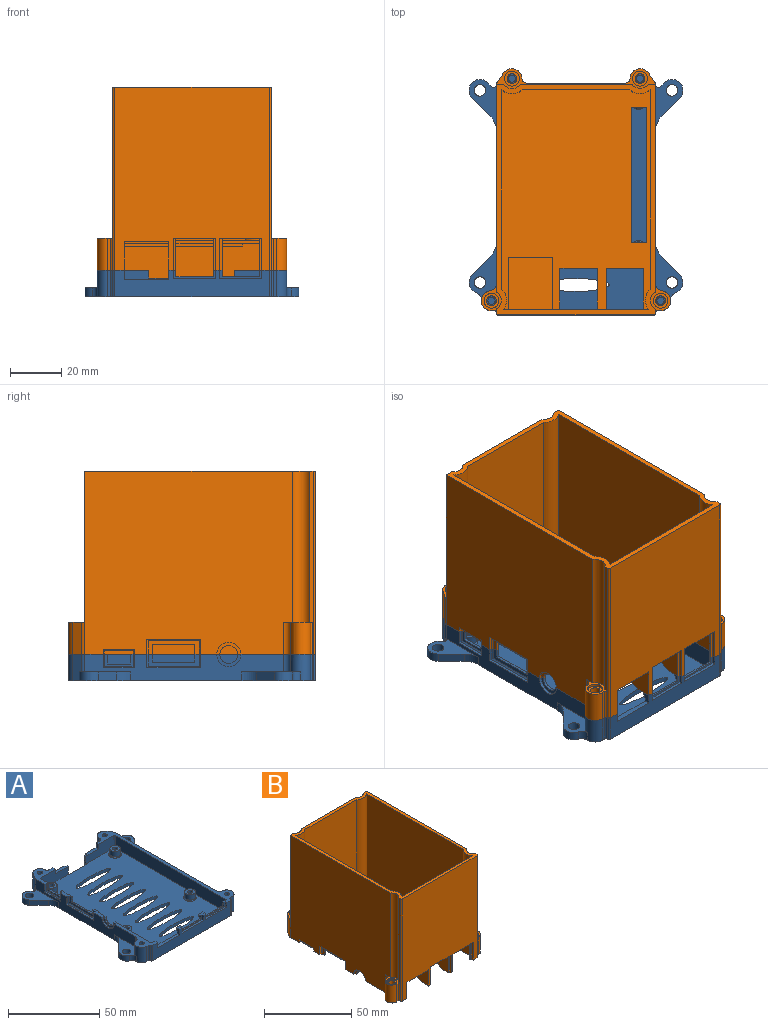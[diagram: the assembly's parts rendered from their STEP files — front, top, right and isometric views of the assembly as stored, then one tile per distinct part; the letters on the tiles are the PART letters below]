
ASSEMBLY  parts=2 mates=1
PART A: 170 faces, bbox 83.8x96.6x10.6 mm
  f0: plane 96.58x83.83mm, normal (0,0,-1), area 5317.9mm2, adj f1,f6,f7,f8,f9,f37,f38,f39
  f1: cylinder r=2.25mm len=4.5mm, axis (0,0,-1), area 49.5mm2, adj f0,f3
  f2: plane 22.79x10.75mm, normal (0,0,1), area 100.2mm2, adj f8,f9,f93,f123,f124,f125,f126,f127
  f3: plane 22.79x10.75mm, normal (0,0,1), area 100.2mm2, adj f1,f39,f152,f153,f154,f155,f156,f157
  f4: plane 20.07x10.76mm, normal (0,0,1), area 93.7mm2, adj f6,f39,f41,f147,f148,f149,f150,f151
  f5: plane 20.07x10.76mm, normal (0,0,1), area 93.7mm2, adj f7,f93,f128,f129,f130,f131,f132,f133
  f6: cylinder r=2.25mm len=4.5mm, axis (0,0,-1), area 49.5mm2, adj f0,f4
  f7: cylinder r=2.25mm len=4.5mm, axis (0,0,-1), area 49.5mm2, adj f0,f5
  f8: cylinder r=2.25mm len=4.5mm, axis (0,0,-1), area 49.5mm2, adj f0,f2
  f9: cylinder r=3.9mm len=10.3mm, axis (0,0,-1), area 101.4mm2, adj f0,f2,f12,f123,f127,f139
  f10: plane 3x2.8mm, normal (0,0,1), area 7.2mm2, adj f25,f28,f30,f37,f162,f163
  f11: plane 3.5x3mm, normal (0,0,1), area 8.1mm2, adj f29,f32,f35,f37,f163,f164,f167,f169
  f12: plane 30.25x10.45mm, normal (0,0,1), area 99.5mm2, adj f9,f22,f26,f37,f89,f90,f91,f92
  f13: plane 8.65x2.5mm, normal (0,0,1), area 15.1mm2, adj f89,f93,f95,f96,f97,f98,f100,f101
  f14: plane 9.75x2.5mm, normal (0,0,1), area 16.8mm2, adj f89,f90,f91,f92,f93,f98,f101,f107
  f15: plane 15.1x14.15mm, normal (0,0,1), area 78mm2, adj f17,f46,f82,f88,f89,f93,f97,f99
  f16: plane 96.25x20.25mm, normal (0,0,1), area 280.9mm2, adj f23,f24,f26,f34,f35,f36,f37,f38
  f17: cylinder r=1.4mm len=8.3mm, axis (0,0,-1), area 73mm2, adj f15,f20
  f18: plane 2.8x2.8mm, normal (0,0,1), area 6.2mm2, adj f22
  f19: plane 2.8x2.8mm, normal (0,0,1), area 6.2mm2, adj f23
  f20: plane 2.8x2.8mm, normal (0,0,1), area 6.2mm2, adj f17
  f21: plane 2.8x2.8mm, normal (0,0,1), area 6.2mm2, adj f24
  f22: cylinder r=1.4mm len=8.3mm, axis (0,0,-1), area 73mm2, adj f12,f18
  f23: cylinder r=1.4mm len=8.3mm, axis (0,0,1), area 73mm2, adj f16,f19
  f24: cylinder r=1.4mm len=8.3mm, axis (0,0,-1), area 73mm2, adj f16,f21
  f25: plane 3.6x3mm, normal (-1,0,0), area 8.7mm2, adj f10,f26,f27,f30,f37,f161
  f26: plane 57x8.3mm, normal (0,1,0), area 322.8mm2, adj f12,f16,f25,f27,f28,f31,f32,f33
  f27: plane 2.8x2mm, normal (0,0.89,-0.45), area 6.3mm2, adj f25,f26,f28,f30
  f28: plane 2.55x1.8mm, normal (1,0,0), area 3.5mm2, adj f10,f26,f27,f30,f163,f168
  f29: plane 3.5x0.55mm, normal (0,1,0), area 1.9mm2, adj f11,f31,f32,f169
  f30: plane 2.8x0.55mm, normal (0,1,0), area 1.5mm2, adj f10,f25,f27,f28
  f31: plane 3.5x2mm, normal (0,0.89,-0.45), area 7.8mm2, adj f26,f29,f32,f169
  f32: plane 2.55x1.8mm, normal (1,0,0), area 3.5mm2, adj f11,f26,f29,f31,f33,f35
  f33: plane 14.5x0.8mm, normal (0,0,1), area 11.6mm2, adj f26,f32,f34,f35
  f34: plane 2.47x0.8mm, normal (-1,0,0), area 2mm2, adj f16,f26,f33,f35
  f35: plane 16.5x3.17mm, normal (0,-1,0), area 16.5mm2, adj f11,f16,f32,f33,f34,f36,f166,f167
  f36: plane 3.17x1.2mm, normal (-1,0,0), area 3.8mm2, adj f16,f35,f37,f166
  f37: plane 60.4x10.3mm, normal (0,-1,0), area 454.9mm2, adj f0,f10,f11,f12,f16,f25,f36,f38
  f38: cylinder r=0.8mm len=10.3mm, axis (0,0,-1), area 12.9mm2, adj f0,f16,f37,f40
  f39: plane 77.46x10.3mm, normal (1,0,0), area 678.5mm2, adj f0,f3,f4,f16,f41,f151,f152,f157
  f40: plane 10.3x0.18mm, normal (1,0,0), area 1.9mm2, adj f0,f16,f38,f159
  f41: cylinder r=2mm len=10.3mm, axis (0,0,1), area 12.1mm2, adj f0,f4,f16,f39,f42,f147
  f42: plane 10.3x3.48mm, normal (0.82,0.58,0), area 43.8mm2, adj f0,f16,f41,f43
  f43: cylinder r=3.9mm len=10.3mm, axis (0,0,-1), area 99.9mm2, adj f0,f16,f42,f44
  f44: cylinder r=2mm len=10.3mm, axis (0,0,1), area 31.5mm2, adj f0,f16,f43,f45
  f45: plane 10.96x10.3mm, normal (0,1,0), area 87.3mm2, adj f0,f16,f44,f47,f83,f84
  f46: plane 10.76x10.3mm, normal (0,1,0), area 85.3mm2, adj f0,f15,f136,f141,f142,f146
  f47: plane 7.3x1mm, normal (-1,0,0), area 7.3mm2, adj f0,f45,f48,f83
  f48: plane 7.3x1.5mm, normal (0,1,0), area 10.9mm2, adj f0,f47,f50,f83
  f49: plane 7.3x1.5mm, normal (0,1,0), area 11mm2, adj f0,f142,f143,f146
  f50: plane 7.3x1mm, normal (-1,0,0), area 7.3mm2, adj f0,f48,f51,f81,f83
  f51: cylinder r=0.5mm len=2mm, axis (0,0,-1), area 1.6mm2, adj f0,f50,f52,f145
  f52: plane 86.93x58.33mm, normal (0,0,1), area 4054.4mm2, adj f26,f51,f53,f54,f55,f56,f57,f58
  f53: extruded ~26x5mm, area 109.1mm2, adj f0,f52
  f54: extruded ~26x5mm, area 109.1mm2, adj f0,f52
  f55: extruded ~26x5mm, area 109.1mm2, adj f0,f52
  f56: extruded ~26x5mm, area 109.1mm2, adj f0,f52
  f57: extruded ~26x5mm, area 109.1mm2, adj f0,f52
  f58: extruded ~26x5mm, area 109.1mm2, adj f0,f52
  f59: extruded ~26x5mm, area 109.1mm2, adj f0,f52
  f60: extruded ~26x5mm, area 109.1mm2, adj f0,f52
  f61: cone r=3.15mm half-angle=45deg, axis (0,0,-1), area 14mm2, adj f52,f62
  f62: cylinder r=2.9mm len=5.8mm, axis (0,0,1), area 63.8mm2, adj f61,f64
  f63: plane 5.8x5.8mm, normal (0,0,1), area 20.3mm2, adj f67,f69
  f64: plane 5.8x5.8mm, normal (0,0,1), area 20.3mm2, adj f62,f74
  f65: plane 5.8x5.8mm, normal (0,0,1), area 20.3mm2, adj f76,f77
  f66: plane 5.8x5.8mm, normal (0,0,1), area 20.3mm2, adj f75,f79
  f67: cylinder r=2.9mm len=5.8mm, axis (0,0,1), area 63.8mm2, adj f63,f68
  f68: cone r=3.15mm half-angle=45deg, axis (0,0,-1), area 14mm2, adj f52,f67
  f69: cylinder r=1.4mm len=5mm, axis (0,0,1), area 44mm2, adj f63,f72
  f70: plane 2.8x2.8mm, normal (0,0,1), area 6.2mm2, adj f74
  f71: plane 2.8x2.8mm, normal (0,0,1), area 6.2mm2, adj f75
  f72: plane 2.8x2.8mm, normal (0,0,1), area 6.2mm2, adj f69
  f73: plane 2.8x2.8mm, normal (0,0,1), area 6.2mm2, adj f76
  f74: cylinder r=1.4mm len=5mm, axis (0,0,1), area 44mm2, adj f64,f70
  f75: cylinder r=1.4mm len=5mm, axis (0,0,1), area 44mm2, adj f66,f71
  f76: cylinder r=1.4mm len=5mm, axis (0,0,1), area 44mm2, adj f65,f73
  f77: cylinder r=2.9mm len=5.8mm, axis (0,0,1), area 63.8mm2, adj f65,f78
  f78: cone r=3.15mm half-angle=45deg, axis (0,0,-1), area 14mm2, adj f52,f77
  f79: cylinder r=2.9mm len=5.8mm, axis (0,0,1), area 63.8mm2, adj f66,f80
  f80: cone r=3.15mm half-angle=45deg, axis (0,0,-1), area 14mm2, adj f52,f79
  f81: plane 21.85x8.3mm, normal (0,-1,0), area 151.4mm2, adj f16,f50,f52,f83,f84,f85
  f82: plane 21.65x8.3mm, normal (0,-1,0), area 149.7mm2, adj f15,f52,f88,f141,f142,f143
  f83: plane 10x2mm, normal (0,0,1), area 18.5mm2, adj f45,f47,f48,f50,f81,f84
  f84: plane 3x2mm, normal (-1,0,0), area 6mm2, adj f16,f45,f81,f83
  f85: cylinder r=0.5mm len=8.3mm, axis (0,0,1), area 6.5mm2, adj f16,f52,f81,f86
  f86: plane 85.6x8.3mm, normal (-1,0,0), area 710.5mm2, adj f16,f52,f85,f87
  f87: cylinder r=0.5mm len=8.3mm, axis (0,0,1), area 6.5mm2, adj f16,f26,f52,f86
  f88: cylinder r=0.5mm len=8.3mm, axis (0,0,1), area 6.5mm2, adj f15,f52,f82,f89
  f89: plane 85.6x8.3mm, normal (1,0,0), area 494.1mm2, adj f12,f13,f14,f15,f52,f88,f90,f102
  f90: cylinder r=3.5mm len=7mm, axis (-1,0,0), area 11mm2, adj f12,f14,f89,f91
  f91: plane 9.5x4.75mm, normal (-1,0,0), area 16.2mm2, adj f12,f14,f90,f92
  f92: cylinder r=4.75mm len=9.5mm, axis (-1,0,0), area 14.9mm2, adj f12,f14,f91,f93
  f93: plane 77.46x10.3mm, normal (-1,0,0), area 472.5mm2, adj f0,f2,f5,f12,f13,f14,f15,f92
  f94: plane 10.3x0.18mm, normal (-1,0,0), area 1.9mm2, adj f0,f12,f137,f138
  f95: plane 5.12x1mm, normal (0,-1,0), area 5.1mm2, adj f13,f93,f96,f121
  f96: plane 5.12x0.5mm, normal (-0.71,-0.71,0), area 3.4mm2, adj f13,f95,f98,f122
  f97: plane 11x4.75mm, normal (-1,0,0), area 18.5mm2, adj f13,f15,f99,f105,f106,f113,f116,f117
  f98: plane 20x4.62mm, normal (-1,0,0), area 40.9mm2, adj f13,f14,f96,f107,f108,f109,f119,f122
  f99: plane 3.75x1mm, normal (0,-1,0), area 3.8mm2, adj f15,f97,f100,f106
  f100: plane 14x5.25mm, normal (1,0,0), area 39.8mm2, adj f13,f15,f99,f102,f103,f104,f105,f106
  f101: plane 23x3.62mm, normal (1,0,0), area 31.8mm2, adj f13,f14,f107,f108,f109,f110,f111,f112
  f102: plane 5.75x0.5mm, normal (0.71,0.71,0), area 3.9mm2, adj f15,f89,f100,f103
  f103: plane 15x0.5mm, normal (0.71,0,-0.71), area 10.3mm2, adj f89,f100,f102,f104
  f104: plane 5.75x0.5mm, normal (0.71,-0.71,0), area 3.9mm2, adj f13,f89,f100,f103
  f105: plane 3.75x1mm, normal (0,1,0), area 3.8mm2, adj f13,f97,f100,f106
  f106: plane 9x1mm, normal (0,0,1), area 9mm2, adj f97,f99,f100,f105
  f107: plane 3.12x1mm, normal (0,1,0), area 3.1mm2, adj f14,f98,f101,f108
  f108: plane 16.5x1mm, normal (0,0,1), area 16.5mm2, adj f98,f101,f107,f109
  f109: plane 3.12x1mm, normal (0,-1,0), area 3.1mm2, adj f13,f98,f101,f108
  f110: plane 4.62x0.5mm, normal (0.71,0.71,0), area 2.9mm2, adj f13,f89,f101,f111
  f111: plane 24x1mm, normal (0.89,0,-0.45), area 26.3mm2, adj f89,f101,f110,f112
  f112: plane 4.62x0.5mm, normal (0.71,-0.71,0), area 2.9mm2, adj f14,f89,f101,f111
  f113: plane 5.25x0.5mm, normal (-0.71,0.71,0), area 3.5mm2, adj f13,f97,f114,f116
  f114: plane 5.25x1mm, normal (0,1,0), area 5.2mm2, adj f13,f93,f113,f115
  f115: plane 12x1mm, normal (0,0,1), area 12mm2, adj f93,f114,f116,f118
  f116: plane 12x0.5mm, normal (-0.71,0,0.71), area 8.1mm2, adj f97,f113,f115,f117
  f117: plane 5.25x0.5mm, normal (-0.71,-0.71,0), area 3.5mm2, adj f15,f97,f116,f118
  f118: plane 5.25x1mm, normal (0,-1,0), area 5.2mm2, adj f15,f93,f115,f117
  f119: plane 5.12x0.5mm, normal (-0.71,0.71,0), area 3.4mm2, adj f14,f98,f120,f122
  f120: plane 5.12x1mm, normal (0,1,0), area 5.1mm2, adj f14,f93,f119,f121
  f121: plane 21x1mm, normal (0,0,1), area 21mm2, adj f93,f95,f120,f122
  f122: plane 21x0.5mm, normal (-0.71,0,0.71), area 14.5mm2, adj f96,f98,f119,f121
  f123: cylinder r=3mm len=6.8mm, axis (0,0,-1), area 29.1mm2, adj f2,f9,f12,f93
  f124: cylinder r=8mm len=5.66mm, axis (0,0,-1), area 22mm2, adj f0,f2,f93,f125
  f125: plane 7.16x7.16mm, normal (-0.71,0.71,0), area 35.5mm2, adj f0,f2,f124,f126
  f126: cylinder r=4.25mm len=7.02mm, axis (0,0,-1), area 30mm2, adj f0,f2,f125,f127
  f127: cylinder r=3mm len=3.5mm, axis (0,0,-1), area 13.4mm2, adj f0,f2,f9,f126
  f128: cylinder r=8mm len=5.66mm, axis (0,0,1), area 22mm2, adj f0,f5,f93,f129
  f129: plane 7.16x7.16mm, normal (-0.71,-0.71,0), area 35.5mm2, adj f0,f5,f128,f130
  f130: cylinder r=4.25mm len=7.26mm, axis (0,0,-1), area 46.7mm2, adj f0,f5,f129,f131
  f131: plane 3.5x1.45mm, normal (0.71,0.71,0), area 7.2mm2, adj f0,f5,f130,f132
  f132: cylinder r=1.2mm len=3.5mm, axis (0,0,-1), area 9.6mm2, adj f0,f5,f131,f133
  f133: cylinder r=2mm len=10.3mm, axis (0,0,-1), area 12.1mm2, adj f0,f5,f15,f93,f132,f134
  f134: plane 10.3x3.48mm, normal (-0.82,0.58,0), area 43.8mm2, adj f0,f15,f133,f135
  f135: cylinder r=3.9mm len=10.3mm, axis (0,0,-1), area 99.9mm2, adj f0,f15,f134,f136
  f136: cylinder r=2mm len=10.3mm, axis (0,0,-1), area 31.5mm2, adj f0,f15,f46,f135
  f137: cylinder r=0.8mm len=10.3mm, axis (0,0,1), area 12.9mm2, adj f0,f12,f37,f94
  f138: cylinder r=0.8mm len=10.3mm, axis (0,0,1), area 12.9mm2, adj f0,f12,f94,f139
  f139: plane 10.3x1.2mm, normal (0,-1,0), area 12.4mm2, adj f0,f9,f12,f138
  f140: cylinder r=0.5mm len=8.3mm, axis (0,0,-1), area 6.5mm2, adj f12,f26,f52,f89
  f141: plane 3x2mm, normal (1,0,0), area 6mm2, adj f15,f46,f82,f142
  f142: plane 10x2mm, normal (0,0,1), area 18.5mm2, adj f46,f49,f82,f141,f143,f146
  f143: plane 7.3x1mm, normal (1,0,0), area 7.3mm2, adj f0,f49,f82,f142,f144
  f144: cylinder r=0.5mm len=2mm, axis (0,0,-1), area 1.6mm2, adj f0,f52,f143,f145
  f145: plane 12.5x2mm, normal (0,1,0), area 25mm2, adj f0,f51,f52,f144
  f146: plane 7.3x1mm, normal (1,0,0), area 7.3mm2, adj f0,f46,f49,f142
  f147: cylinder r=1.2mm len=3.5mm, axis (0,0,1), area 9.6mm2, adj f0,f4,f41,f148
  f148: plane 3.5x1.45mm, normal (-0.71,0.71,0), area 7.2mm2, adj f0,f4,f147,f149
  f149: cylinder r=4.25mm len=7.26mm, axis (0,0,-1), area 46.7mm2, adj f0,f4,f148,f150
  f150: plane 7.16x7.16mm, normal (0.71,-0.71,0), area 35.5mm2, adj f0,f4,f149,f151
  f151: cylinder r=8mm len=5.66mm, axis (0,0,-1), area 22mm2, adj f0,f4,f39,f150
  f152: cylinder r=8mm len=5.66mm, axis (0,0,1), area 22mm2, adj f0,f3,f39,f153
  f153: plane 7.16x7.16mm, normal (0.71,0.71,0), area 35.5mm2, adj f0,f3,f152,f154
  f154: cylinder r=4.25mm len=7.02mm, axis (0,0,-1), area 30mm2, adj f0,f3,f153,f155
  f155: cylinder r=3mm len=3.5mm, axis (0,0,1), area 13.4mm2, adj f0,f3,f154,f156
  f156: cylinder r=3.9mm len=10.3mm, axis (0,0,1), area 101.4mm2, adj f0,f3,f16,f155,f157,f158
  f157: cylinder r=3mm len=6.8mm, axis (0,0,1), area 29.1mm2, adj f3,f16,f39,f156
  f158: plane 10.3x1.2mm, normal (0,-1,0), area 12.4mm2, adj f0,f16,f156,f159
  f159: cylinder r=0.8mm len=10.3mm, axis (0,0,-1), area 12.9mm2, adj f0,f16,f40,f158
  f160: plane 3.6x2mm, normal (1,0,0), area 7.2mm2, adj f12,f26,f37,f161
  f161: plane 17.4x2mm, normal (0,0,1), area 34.8mm2, adj f25,f26,f37,f160
  f162: plane 3.17x1.2mm, normal (1,0,0), area 3.8mm2, adj f10,f37,f163,f165
  f163: plane 16.5x3.17mm, normal (0,-1,0), area 16.5mm2, adj f10,f11,f28,f162,f164,f165,f168,f169
  f164: plane 3.17x1.2mm, normal (-1,0,0), area 3.8mm2, adj f11,f37,f163,f165
  f165: plane 16.5x1.2mm, normal (0,0,1), area 19.8mm2, adj f37,f162,f163,f164
  f166: plane 16.5x1.2mm, normal (0,0,1), area 19.8mm2, adj f35,f36,f37,f167
  f167: plane 3.17x1.2mm, normal (1,0,0), area 3.8mm2, adj f11,f35,f37,f166
  f168: plane 14.5x0.8mm, normal (0,0,1), area 11.6mm2, adj f26,f28,f163,f169
  f169: plane 2.55x1.8mm, normal (-1,0,0), area 3.5mm2, adj f11,f26,f29,f31,f163,f168
PART B: 138 faces, bbox 73.8x96.3x74.5 mm
  f0: plane 86.6x58mm, normal (0,0,-1), area 1541.9mm2, adj f1,f2,f3,f4,f5,f6,f11,f12
  f1: plane 14.5x1mm, normal (0,-1,0), area 14.5mm2, adj f0,f49,f55,f124
  f2: plane 14.5x1mm, normal (0,-1,0), area 14.5mm2, adj f0,f57,f62,f124
  f3: plane 6x1mm, normal (0,1,0), area 6mm2, adj f0,f4,f6,f124
  f4: plane 52.7x1mm, normal (1,0,0), area 52.7mm2, adj f0,f3,f5,f124
  f5: plane 6x1mm, normal (0,-1,0), area 6mm2, adj f0,f4,f6,f124
  f6: plane 52.7x1mm, normal (-1,0,0), area 52.7mm2, adj f0,f3,f5,f124
  f7: plane 89.97x62mm, normal (0,0,1), area 599.4mm2, adj f38,f39,f44,f45,f64,f65,f66,f115
  f8: plane 62x7.85mm, normal (0,0,1), area 83.3mm2, adj f27,f34,f35,f36,f37,f95,f96,f97
  f9: plane 11.53x7.82mm, normal (0,0,1), area 24.2mm2, adj f38,f39,f40,f41,f42,f43,f110,f121
  f10: plane 11.53x7.79mm, normal (0,0,1), area 23.9mm2, adj f65,f66,f67,f68,f69,f70,f111,f115
  f11: cylinder r=1mm len=10.5mm, axis (0,0,-1), area 16.5mm2, adj f0,f12,f15,f20
  f12: plane 10.5x1.55mm, normal (0,1,0), area 16.3mm2, adj f0,f11,f15,f53
  f13: plane 10.5x1.75mm, normal (0,1,0), area 18.4mm2, adj f0,f16,f25,f62
  f14: plane 9.75x2.5mm, normal (0,0,-1), area 16.8mm2, adj f20,f65,f71,f72,f73,f74,f75,f76
  f15: plane 30.25x10.45mm, normal (0,0,-1), area 94.5mm2, adj f11,f12,f20,f45,f53,f64,f65,f66
  f16: plane 96.25x20.3mm, normal (0,0,-1), area 270.9mm2, adj f13,f22,f23,f24,f25,f26,f27,f34
  f17: plane 32.75x14.2mm, normal (0,0,-1), area 96.1mm2, adj f20,f21,f22,f27,f33,f65,f76,f77
  f18: plane 6x3.5mm, normal (0,0,-1), area 18.6mm2, adj f45,f46,f48,f55,f56,f57,f58,f60
  f19: plane 6x2.8mm, normal (0,0,-1), area 15.6mm2, adj f45,f47,f49,f50,f51,f63
  f20: plane 84.6x10.5mm, normal (1,0,0), area 682.2mm2, adj f0,f11,f14,f15,f17,f21,f73,f83
  f21: cylinder r=1mm len=10.5mm, axis (0,0,1), area 16.5mm2, adj f0,f17,f20,f22
  f22: plane 56x13.5mm, normal (0,-1,0), area 688.2mm2, adj f0,f16,f17,f21,f23,f26,f29,f33
  f23: cylinder r=1mm len=10.5mm, axis (0,0,1), area 16.5mm2, adj f0,f16,f22,f24
  f24: plane 84.6x10.5mm, normal (-1,0,0), area 888.3mm2, adj f0,f16,f23,f25
  f25: cylinder r=1mm len=10.5mm, axis (0,0,1), area 16.5mm2, adj f0,f13,f16,f24
  f26: plane 3x2mm, normal (1,0,0), area 6mm2, adj f16,f22,f27,f29
  f27: plane 38.21x15.5mm, normal (0,1,0), area 553.1mm2, adj f8,f16,f17,f26,f28,f29,f31,f32
  f28: plane 1.5x1mm, normal (1,0,0), area 1.5mm2, adj f27,f29,f30,f32
  f29: plane 33.4x2mm, normal (0,0,-1), area 50.3mm2, adj f22,f26,f27,f28,f30,f31,f33
  f30: plane 16.5x1.5mm, normal (0,1,0), area 24.7mm2, adj f28,f29,f31,f32
  f31: plane 1.5x1mm, normal (-1,0,0), area 1.5mm2, adj f27,f29,f30,f32
  f32: plane 16.5x1mm, normal (0,0,-1), area 16.5mm2, adj f27,f28,f30,f31
  f33: plane 3x2mm, normal (-1,0,0), area 6mm2, adj f17,f22,f27,f29
  f34: cylinder r=2mm len=12.5mm, axis (0,0,1), area 38.2mm2, adj f8,f16,f27,f35
  f35: cylinder r=3.9mm len=12.5mm, axis (0,0,1), area 121.2mm2, adj f8,f16,f34,f36
  f36: plane 12.5x3.48mm, normal (0.82,0.58,0), area 53.1mm2, adj f8,f16,f35,f37
  f37: cylinder r=2mm len=12.5mm, axis (0,0,1), area 15.3mm2, adj f8,f16,f36,f38
  f38: plane 80.91x71.5mm, normal (1,0,0), area 5742mm2, adj f7,f9,f16,f37,f40,f120,f121
  f39: plane 71.5x1.5mm, normal (1,0,0), area 91mm2, adj f7,f9,f16,f43,f44,f121
  f40: cylinder r=3mm len=12.5mm, axis (0,0,1), area 53.5mm2, adj f9,f16,f38,f41
  f41: cylinder r=3.9mm len=12.5mm, axis (0,0,1), area 146.1mm2, adj f9,f16,f40,f42
  f42: plane 12.5x1.2mm, normal (0,-1,0), area 15mm2, adj f9,f16,f41,f43
  f43: cylinder r=0.8mm len=12.5mm, axis (0,0,-1), area 15.7mm2, adj f9,f16,f39,f42
  f44: cylinder r=0.8mm len=71.5mm, axis (0,0,-1), area 89.8mm2, adj f7,f16,f39,f45
  f45: plane 71.5x60.4mm, normal (0,-1,0), area 3709.5mm2, adj f7,f15,f16,f18,f19,f44,f46,f51
  f46: plane 12.5x1.2mm, normal (-1,0,0), area 15mm2, adj f18,f45,f48,f123
  f47: plane 12.5x1mm, normal (0,-1,0), area 12.5mm2, adj f19,f49,f63,f123
  f48: plane 12.5x1mm, normal (0,-1,0), area 12.5mm2, adj f18,f46,f55,f123
  f49: plane 25.8x12.5mm, normal (1,0,0), area 178.5mm2, adj f0,f1,f19,f47,f50,f123,f124,f125
  f50: plane 21x10.5mm, normal (0,0.45,-0.89), area 65.7mm2, adj f0,f19,f49,f51
  f51: plane 27x11.3mm, normal (-1,0,0), area 191.4mm2, adj f0,f19,f45,f50,f52,f54
  f52: plane 17.4x0.8mm, normal (0,-1,0), area 13.9mm2, adj f0,f51,f53,f54
  f53: plane 22.7x11.3mm, normal (1,0,0), area 39.2mm2, adj f0,f12,f15,f45,f52,f54
  f54: plane 22.7x17.4mm, normal (0,0,-1), area 395mm2, adj f45,f51,f52,f53
  f55: plane 25.8x12.5mm, normal (-1,0,0), area 178.5mm2, adj f0,f1,f18,f48,f56,f123,f124,f125
  f56: plane 21x10.5mm, normal (0,0.45,-0.89), area 82.2mm2, adj f0,f18,f55,f57
  f57: plane 25.8x12.5mm, normal (1,0,0), area 178.5mm2, adj f0,f2,f18,f56,f58,f122,f124,f125
  f58: plane 12.5x1mm, normal (0,-1,0), area 12.5mm2, adj f18,f57,f60,f122
  f59: plane 12.5x1mm, normal (0,-1,0), area 12.5mm2, adj f16,f61,f62,f122
  f60: plane 12.5x1.2mm, normal (1,0,0), area 15mm2, adj f18,f45,f58,f122
  f61: plane 12.5x1.2mm, normal (-1,0,0), area 15mm2, adj f16,f45,f59,f122
  f62: plane 17.05x12.5mm, normal (-1,0,0), area 26.2mm2, adj f0,f2,f13,f16,f59,f122,f124,f125
  f63: plane 12.5x1.2mm, normal (1,0,0), area 15mm2, adj f19,f45,f47,f123
  f64: cylinder r=0.8mm len=71.5mm, axis (0,0,1), area 89.8mm2, adj f7,f15,f45,f66
  f65: plane 80.95x71.5mm, normal (-1,0,0), area 5560.3mm2, adj f7,f10,f14,f15,f17,f67,f71,f74
  f66: plane 71.5x1.54mm, normal (-1,0,0), area 93.3mm2, adj f7,f10,f15,f64,f70,f115
  f67: cylinder r=3mm len=12.5mm, axis (0,0,-1), area 53.5mm2, adj f10,f15,f65,f68
  f68: cylinder r=3.9mm len=12.5mm, axis (0,0,1), area 146.1mm2, adj f10,f15,f67,f69
  f69: plane 12.5x1.2mm, normal (0,-1,0), area 15mm2, adj f10,f15,f68,f70
  f70: cylinder r=0.8mm len=12.5mm, axis (0,0,1), area 15.7mm2, adj f10,f15,f66,f69
  f71: cylinder r=4.75mm len=9.5mm, axis (-1,0,0), area 14.9mm2, adj f14,f15,f65,f72
  f72: plane 9.5x4.75mm, normal (-1,0,0), area 16.2mm2, adj f14,f15,f71,f73
  f73: cylinder r=3.5mm len=7mm, axis (-1,0,0), area 11mm2, adj f14,f15,f20,f72
  f74: plane 5.93x1mm, normal (0,1,0), area 5.9mm2, adj f14,f65,f75,f79
  f75: plane 5.93x0.5mm, normal (-0.71,0.71,0), area 4mm2, adj f14,f74,f76,f80
  f76: plane 20x5.43mm, normal (-1,0,0), area 43.8mm2, adj f14,f17,f75,f77,f80,f81,f86,f87
  f77: plane 5.93x0.5mm, normal (-0.71,-0.71,0), area 4mm2, adj f17,f76,f78,f80
  f78: plane 5.93x1mm, normal (0,-1,0), area 5.9mm2, adj f17,f65,f77,f79
  f79: plane 21x1mm, normal (0,0,-1), area 21mm2, adj f65,f74,f78,f80
  f80: plane 21x0.5mm, normal (-0.71,0,-0.71), area 14.5mm2, adj f75,f76,f77,f79
  f81: plane 3.93x1mm, normal (0,1,0), area 3.9mm2, adj f14,f76,f82,f87
  f82: plane 23x5.93mm, normal (1,0,0), area 71.5mm2, adj f14,f17,f81,f83,f84,f85,f86,f87
  f83: plane 6.43x0.5mm, normal (0.71,-0.71,0), area 4.4mm2, adj f14,f20,f82,f84
  f84: plane 24x0.5mm, normal (0.71,0,0.71), area 16.6mm2, adj f20,f82,f83,f85
  f85: plane 6.43x0.5mm, normal (0.71,0.71,0), area 4.4mm2, adj f17,f20,f82,f84
  f86: plane 3.93x1mm, normal (0,-1,0), area 3.9mm2, adj f17,f76,f82,f87
  f87: plane 16.5x1mm, normal (0,0,-1), area 16.5mm2, adj f76,f81,f82,f86
  f88: plane 2x1mm, normal (0,1,0), area 2mm2, adj f17,f65,f89,f93
  f89: plane 2x0.5mm, normal (-0.71,0.71,0), area 1.2mm2, adj f17,f88,f90,f94
  f90: plane 11x1.5mm, normal (-1,0,0), area 16.5mm2, adj f17,f89,f91,f94
  f91: plane 2x0.5mm, normal (-0.71,-0.71,0), area 1.2mm2, adj f17,f90,f92,f94
  f92: plane 2x1mm, normal (0,-1,0), area 2mm2, adj f17,f65,f91,f93
  f93: plane 12x1mm, normal (0,0,-1), area 12mm2, adj f65,f88,f92,f94
  f94: plane 12x0.5mm, normal (-0.71,0,-0.71), area 8.1mm2, adj f89,f90,f91,f93
  f95: cylinder r=2mm len=12.5mm, axis (0,0,-1), area 15.3mm2, adj f8,f17,f65,f96
  f96: plane 12.5x3.48mm, normal (-0.82,0.58,0), area 53.1mm2, adj f8,f17,f95,f97
  f97: cylinder r=3.9mm len=12.5mm, axis (0,0,1), area 121.2mm2, adj f8,f17,f96,f98
  f98: cylinder r=2mm len=12.5mm, axis (0,0,-1), area 38.2mm2, adj f8,f17,f27,f97
  f99: plane 2.5x0.5mm, normal (0.71,0.71,0), area 1.6mm2, adj f17,f20,f100,f102
  f100: plane 12x2mm, normal (1,0,0), area 24mm2, adj f17,f99,f101,f102
  f101: plane 2.5x0.5mm, normal (0.71,-0.71,0), area 1.6mm2, adj f17,f20,f100,f102
  f102: plane 13x0.5mm, normal (0.71,0,0.71), area 8.8mm2, adj f20,f99,f100,f101
  f103: cylinder r=1.9mm len=11.5mm, axis (0,0,1), area 137.3mm2, adj f16,f106
  f104: plane 5.8x5.8mm, normal (0,0,1), area 15.1mm2, adj f108,f114
  f105: plane 5.8x5.8mm, normal (0,0,1), area 15.1mm2, adj f109,f113
  f106: plane 5.8x5.8mm, normal (0,0,1), area 15.1mm2, adj f103,f110
  f107: plane 5.8x5.8mm, normal (0,0,1), area 15.1mm2, adj f111,f112
  f108: cylinder r=2.9mm len=5.8mm, axis (0,0,1), area 18.2mm2, adj f8,f104
  f109: cylinder r=2.9mm len=5.8mm, axis (0,0,1), area 18.2mm2, adj f8,f105
  f110: cylinder r=2.9mm len=5.8mm, axis (0,0,1), area 18.2mm2, adj f9,f106
  f111: cylinder r=2.9mm len=5.8mm, axis (0,0,1), area 18.2mm2, adj f10,f107
  f112: cylinder r=1.9mm len=11.5mm, axis (0,0,1), area 137.3mm2, adj f15,f107
  f113: cylinder r=1.9mm len=11.5mm, axis (0,0,-1), area 137.3mm2, adj f16,f105
  f114: cylinder r=1.9mm len=11.5mm, axis (0,0,-1), area 137.3mm2, adj f17,f104
  f115: cylinder r=3.89mm len=59mm, axis (0,0,-1), area 473.2mm2, adj f7,f10,f65,f66
  f116: plane 59x2.85mm, normal (0,1,0), area 168.3mm2, adj f7,f8,f65,f117
  f117: cylinder r=3.95mm len=59mm, axis (0,0,-1), area 429.9mm2, adj f7,f8,f116,f118
  f118: plane 59x43.73mm, normal (0,1,0), area 2580.3mm2, adj f7,f8,f117,f119
  f119: cylinder r=3.92mm len=59mm, axis (0,0,-1), area 425.2mm2, adj f7,f8,f118,f120
  f120: plane 59x2.88mm, normal (0,1,0), area 170mm2, adj f7,f8,f38,f119
  f121: cylinder r=3.92mm len=59mm, axis (0,0,-1), area 479.8mm2, adj f7,f9,f38,f39
  f122: plane 16.5x2mm, normal (0,0,-1), area 31.4mm2, adj f45,f57,f58,f59,f60,f61,f62,f125
  f123: plane 16.5x2mm, normal (0,0,-1), area 31.4mm2, adj f45,f46,f47,f48,f49,f55,f63,f125
  f124: plane 85.98x58mm, normal (0,0,1), area 4159.1mm2, adj f1,f2,f3,f4,f5,f6,f49,f55
  f125: plane 60x56.76mm, normal (0,1,0), area 3376.5mm2, adj f7,f49,f55,f57,f62,f122,f123,f124
  f126: cylinder r=5.89mm len=60mm, axis (0,0,1), area 529.8mm2, adj f7,f124,f125,f132
  f127: cylinder r=5.92mm len=60mm, axis (0,0,1), area 533.1mm2, adj f7,f124,f125,f128
  f128: plane 77.93x60mm, normal (-1,0,0), area 4675.8mm2, adj f7,f124,f127,f129
  f129: cylinder r=5.92mm len=60mm, axis (0,0,1), area 525.8mm2, adj f7,f124,f128,f130
  f130: plane 60x41.99mm, normal (0,-1,0), area 2519.6mm2, adj f7,f124,f129,f131
  f131: cylinder r=5.95mm len=60mm, axis (0,0,1), area 528.1mm2, adj f7,f124,f130,f132
  f132: plane 77.94x60mm, normal (1,0,0), area 4676.6mm2, adj f7,f124,f126,f131
  f133: plane 46.98x46.29mm, normal (0,0,-1), area 2174.9mm2, adj f134,f135,f136,f137
  f134: plane 46.98x1mm, normal (0,1,0), area 47mm2, adj f0,f133,f135,f137
  f135: plane 46.29x1mm, normal (1,0,0), area 46.3mm2, adj f0,f133,f134,f136
  f136: plane 46.98x1mm, normal (0,-1,0), area 47mm2, adj f0,f133,f135,f137
  f137: plane 46.29x1mm, normal (-1,0,0), area 46.3mm2, adj f0,f133,f134,f136
PLACE A t=(1.46,-16.28,4.26)mm
PLACE B t=(1.46,-16.28,25.06)mm
MATE fastened B.f68 <-> A.f9  axis (0,0,-1) through (-0.54,-6.2,14.56)mm
